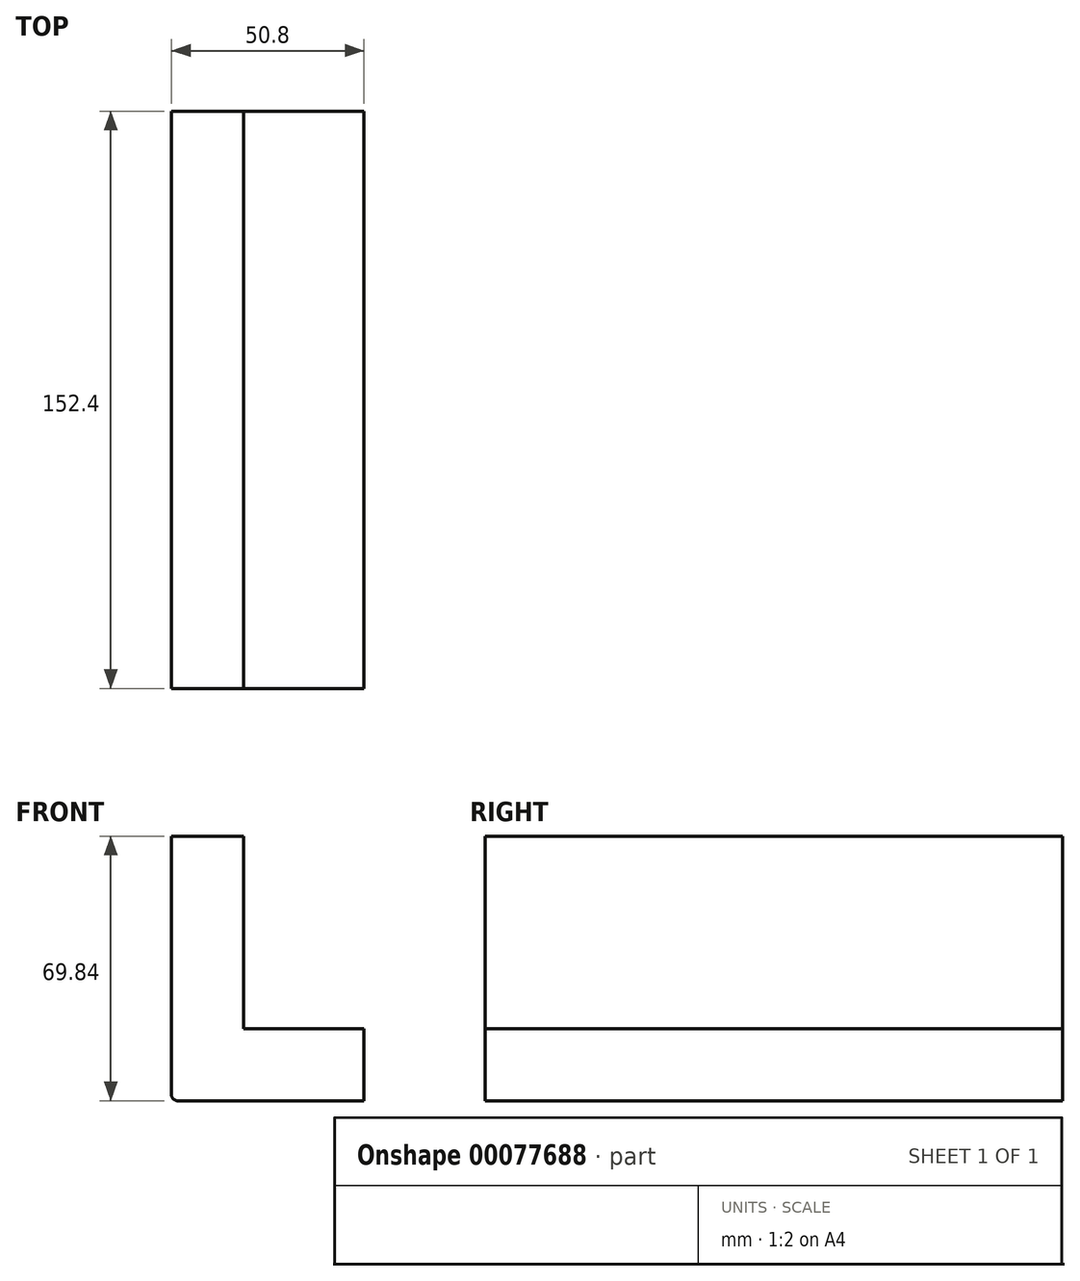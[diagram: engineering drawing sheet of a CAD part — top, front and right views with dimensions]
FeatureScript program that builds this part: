
annotation { "Feature Type Name" : "Feature", "Feature Type Description" : "" }
export const myFeature = defineFeature(function(context is Context, id is Id, definition is map)
    precondition{}
    {
        {
            var Q0;
            Q0=qCreatedBy(makeId("Front.planeOp"),FACE);
            var sketch = newSketch(context, id + "F0", { "sketchPlane" : qUnion([Q0])});
            skLineSegment(sketch, "E0", {"start": v(-23.81, -34.93) * mm, "end": v(25.4, -34.93) * mm});
            skLineSegment(sketch, "E1", {"start": v(-25.4, -15.88) * mm, "end": v(-25.4, -33.34) * mm});
            skLineSegment(sketch, "E2", {"start": v(25.4, -15.88) * mm, "end": v(-25.4, -15.88) * mm});
            skLineSegment(sketch, "E3", {"start": v(25.4, -34.93) * mm, "end": v(25.4, -15.88) * mm});
            skLineSegment(sketch, "E4", {"start": v(-6.35, -15.88) * mm, "end": v(-6.35, 34.93) * mm});
            skLineSegment(sketch, "E5", {"start": v(-6.35, 34.93) * mm, "end": v(-25.4, 34.93) * mm});
            skLineSegment(sketch, "E6", {"start": v(-25.4, 34.93) * mm, "end": v(-25.4, -15.88) * mm});
            skLineSegment(sketch, "E7", {"start": v(-25.4, -15.88) * mm, "end": v(-6.35, -15.88) * mm});
            skArc(sketch, "E8", {"start": v(-25.4, -33.34) * mm, "mid": v(-24.94, -34.46) * mm, "end": v(-23.81, -34.93) * mm});
            skSolve(sketch);
        }
        {
            var Q0;
            Q0=makeQuery(id+"F0.imprint","IMPRINT",FACE,{"disambiguationData":[TD([[makeQuery(id+"F0.imprint","IMPRINT",EDGE,{"derivedFrom":sQuery(id+"F0.wireOp",EDGE,"E4")}),1.0]])]});
            var Q1;
            Q1=makeQuery(id+"F0.imprint","IMPRINT",FACE,{"disambiguationData":[TD([[makeQuery(id+"F0.imprint","IMPRINT",EDGE,{"derivedFrom":sQuery(id+"F0.wireOp",EDGE,"E0")}),1.0]])]});
            extrude(context, id + "F1", {"entities" : qUnion([Q0, Q1]), "depth" : 152.4 * mm});
        }
    });
